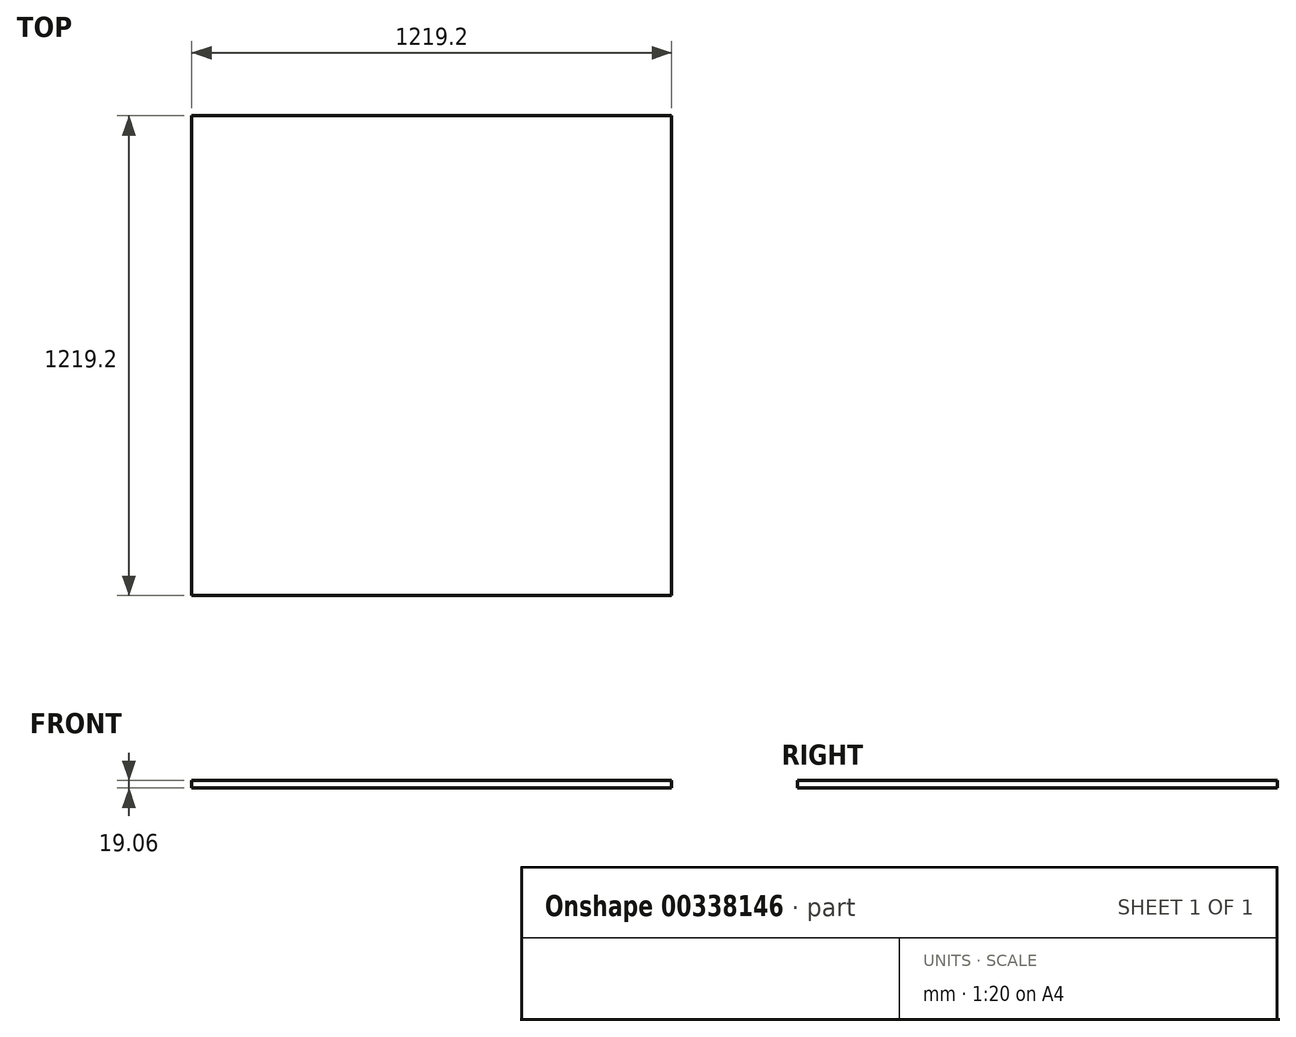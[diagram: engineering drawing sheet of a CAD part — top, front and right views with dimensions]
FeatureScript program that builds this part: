
annotation { "Feature Type Name" : "Feature", "Feature Type Description" : "" }
export const myFeature = defineFeature(function(context is Context, id is Id, definition is map)
    precondition{}
    {
        {
            var Q0;
            Q0=qCreatedBy(makeId("Top.planeOp"),FACE);
            var sketch = newSketch(context, id + "F0", { "sketchPlane" : qUnion([Q0])});
            skLineSegment(sketch, "E0.bottom", {"start": v(609.6, 609.6) * mm, "end": v(-609.6, 609.6) * mm});
            skLineSegment(sketch, "E0.top", {"start": v(609.6, -609.6) * mm, "end": v(-609.6, -609.6) * mm});
            skLineSegment(sketch, "E0.left", {"start": v(609.6, 609.6) * mm, "end": v(609.6, -609.6) * mm});
            skLineSegment(sketch, "E0.right", {"start": v(-609.6, 609.6) * mm, "end": v(-609.6, -609.6) * mm});
            skPoint(sketch, "E0.middle", {"position": v(0, 0) * mm});
            skSolve(sketch);
        }
        {
            var Q0;
            Q0=makeQuery(id+"F0.imprint","IMPRINT",FACE,{"disambiguationData":[TD([[makeQuery(id+"F0.imprint","IMPRINT",EDGE,{"derivedFrom":sQuery(id+"F0.wireOp",EDGE,"E0.bottom")}),1.0]])]});
            extrude(context, id + "F1", {"entities" : qUnion([Q0]), "endBound" : BoundingType.SYMMETRIC, "depth" : 19.05 * mm});
        }
    });
